# Revit family: PRD_AR_WstBns_RODANWasteBin_RODX605EE
name_source: partatom
category: Specialty Equipment
revit_build: Autodesk Revit 2018 (Build: 20190510_1515(x64)
units: mm (PartAtom-declared; Revit-internal decimal feet)

## family parameters
Cut with Voids When Loaded = Yes
Host = Face
OmniClass Number = 23.40.20.31.11
OmniClass Title = Bins
Part Type = Normal
Room Calculation Point = No
Round Connector Dimension = Use Diameter
Shared = No

## types (1)
- RODX605EE
    AssetType = Fixed
    BIMObjectName = PRD_AR_WasteBins_RODANWasteBin_RODX605EE
    BagHolder = Optional
    Category = Pr_40_50_07_96, Waste bins
    Default Elevation = 850 mm  [stored 2.78871 ft]
    Description = Waste bin for recessed mounting, stainless steel, surface satin finished, material thickness 0.8 mm, rounded edges, cylinder lock with KWC standard key, mounting with in-wall frame, includes stainless steel screws and dowels. Approx. 23 liter capacity, full recessed version
    DurationUnit = year
    Features = stainless steel, surface satin finished
    FillingVolume = 23.00 liter
    Finish = satin finished
    GrossWeight = 9.90 kg
    IfcExportAs = IfcFurnitureType
    IfcExportType = USERDEFINED
    IntegralAccessories = incl. stainless steel screws and dowels
    IsBuiltIn = TRUE
    Lid = No
    Lock = Key-lock
    MainColor = stainless steel
    Manufacturer = KWC Group AG
    ManufacturerName = KWC Group AG
    ManufacturerURL = www.kwc.com
    Material = stainless steel
    MaterialCode = 1.4301
    MaterialThickness = 0.80 mm
    Model = RODX605EE
    ModelNumber = 2000101344
    ModelReference = RODX605EE
    NBSDescription = Waste bins
    NBSReference = 45-35-72/380
    Name = Waste Bin RODX605EE
    NetWeight = 8.32 kg
    NominalDepth = 171 mm  [stored 0.561024 ft]
    NominalHeight = 690 mm  [stored 2.26378 ft]
    NominalWidth = 410 mm  [stored 1.34514 ft]
    ProductInformation = https://pim.kwc.com
    Size = 410 x 690 x 171 mm
    Style = waste bin
    TypeOfFixing = Screw
    TypeOfMounting = Recessed mounting
    URL = www.kwc.com
    Uniclass2015Code = Pr_40_50_07_96
    Uniclass2015Title = Waste bins
    Uniclass2015Version = Products v1.10
    Version = 1
    WarrantyDurationUnit = year
    WasteBinMaterial = PRD_AR_StainlessSteel_SatinFinished

note: [stored X ft] marks values corroborated as IEEE doubles in the binary element streams (Revit-internal decimal feet)

## geometry (parser evidence)
native form markers: Sweep x3
no freeform markers — native parametric forms only
